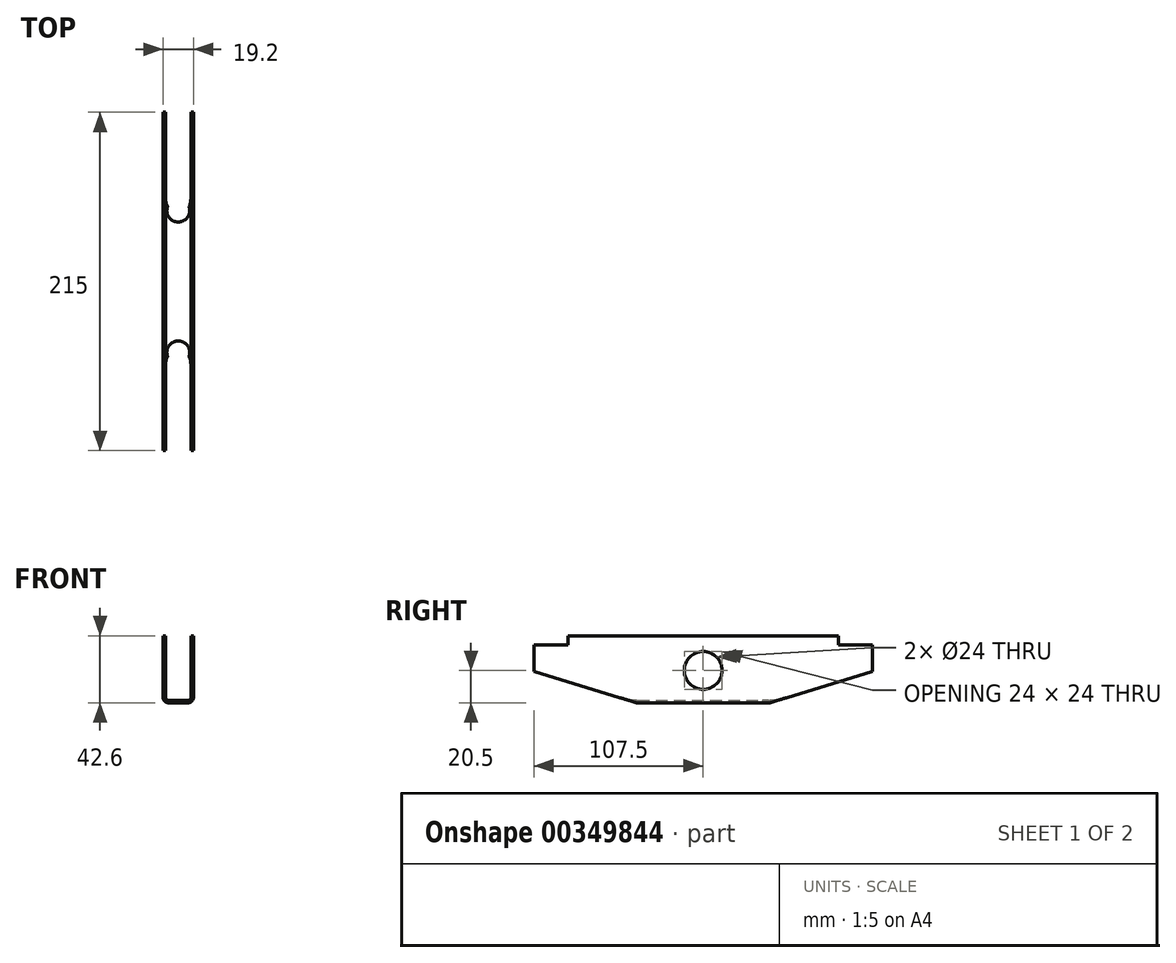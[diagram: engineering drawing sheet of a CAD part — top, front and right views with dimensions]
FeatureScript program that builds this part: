
annotation { "Feature Type Name" : "Feature", "Feature Type Description" : "" }
export const myFeature = defineFeature(function(context is Context, id is Id, definition is map)
    precondition{}
    {
        {
            var Q0;
            Q0=qCreatedBy(makeId("Front.planeOp"),FACE);
            var sketch = newSketch(context, id + "F0", { "sketchPlane" : qUnion([Q0])});
            skLineSegment(sketch, "E0", {"start": v(0, 0) * mm, "end": v(-6.4, 0) * mm});
            skLineSegment(sketch, "E1", {"start": v(-9.6, 3.2) * mm, "end": v(-9.6, 42.6) * mm});
            skLineSegment(sketch, "E2", {"start": v(-9.6, 42.6) * mm, "end": v(-8, 42.6) * mm});
            skLineSegment(sketch, "E3", {"start": v(-8, 42.6) * mm, "end": v(-8, 3.2) * mm});
            skLineSegment(sketch, "E4", {"start": v(-6.4, 1.6) * mm, "end": v(0, 1.6) * mm});
            skPoint(sketch, "E5.visualSharp", {"position": v(-8, 1.6) * mm});
            skArc(sketch, "E5.filletArc", {"start": v(-8, 3.2) * mm, "mid": v(-7.53, 2.07) * mm, "end": v(-6.4, 1.6) * mm});
            skPoint(sketch, "E6.visualSharp", {"position": v(-9.6, 0) * mm});
            skArc(sketch, "E6.filletArc", {"start": v(-9.6, 3.2) * mm, "mid": v(-8.66, 0.94) * mm, "end": v(-6.4, 0) * mm});
            skLineSegment(sketch, "E7", {"start": v(0, 0) * mm, "end": v(0, 33.76) * mm, "construction": true});
            skLineSegment(sketch, "E8.MirrorCS", {"start": v(9.6, 42.6) * mm, "end": v(8, 42.6) * mm});
            skArc(sketch, "E9.MirrorCS", {"start": v(8, 3.2) * mm, "mid": v(7.53, 2.07) * mm, "end": v(6.4, 1.6) * mm});
            skArc(sketch, "E10.MirrorCS", {"start": v(9.6, 3.2) * mm, "mid": v(8.66, 0.94) * mm, "end": v(6.4, 0) * mm});
            skLineSegment(sketch, "E11.MirrorCS", {"start": v(0, 0) * mm, "end": v(6.4, 0) * mm});
            skLineSegment(sketch, "E12.MirrorCS", {"start": v(9.6, 3.2) * mm, "end": v(9.6, 42.6) * mm});
            skPoint(sketch, "E13.MirrorP", {"position": v(8, 1.6) * mm});
            skPoint(sketch, "E14.MirrorP", {"position": v(9.6, 0) * mm});
            skLineSegment(sketch, "E15.MirrorCS", {"start": v(8, 42.6) * mm, "end": v(8, 3.2) * mm});
            skLineSegment(sketch, "E16.MirrorCS", {"start": v(6.4, 1.6) * mm, "end": v(0, 1.6) * mm});
            skSolve(sketch);
        }
        {
            var Q0;
            Q0 = qSketchRegion(id + "F0", true);
            extrude(context, id + "F1", {"entities" : qUnion([Q0]), "endBound" : BoundingType.SYMMETRIC, "depth" : 215 * mm});
        }
        {
            var Q0;
            Q0=makeQuery(id+"F1.opExtrude","SWEPT_FACE",FACE,{"disambiguationData":[OSD([sQuery(id+"F0.wireOp",EDGE,"E1")])]});
            var sketch = newSketch(context, id + "F2", { "sketchPlane" : qUnion([Q0])});
            skLineSegment(sketch, "E17.bottom", {"start": v(-107.5, 42.6) * mm, "end": v(-86, 42.6) * mm});
            skLineSegment(sketch, "E17.top", {"start": v(-107.5, 36.6) * mm, "end": v(-86, 36.6) * mm});
            skLineSegment(sketch, "E17.left", {"start": v(-107.5, 42.6) * mm, "end": v(-107.5, 36.6) * mm});
            skLineSegment(sketch, "E17.right", {"start": v(-86, 42.6) * mm, "end": v(-86, 36.6) * mm});
            skLineSegment(sketch, "E18", {"start": v(-107.5, 20) * mm, "end": v(-42.5, 0) * mm});
            skLineSegment(sketch, "E19", {"start": v(-42.5, 0) * mm, "end": v(-107.5, 0) * mm});
            skLineSegment(sketch, "E20", {"start": v(-107.5, 0) * mm, "end": v(-107.5, 20) * mm});
            skLineSegment(sketch, "E21", {"start": v(0, 0) * mm, "end": v(0, 57.1) * mm, "construction": true});
            skLineSegment(sketch, "E22.MirrorCS", {"start": v(107.5, 0) * mm, "end": v(107.5, 20) * mm});
            skLineSegment(sketch, "E23.MirrorCS", {"start": v(42.5, 0) * mm, "end": v(107.5, 0) * mm});
            skLineSegment(sketch, "E24.MirrorCS", {"start": v(107.5, 20) * mm, "end": v(42.5, 0) * mm});
            skLineSegment(sketch, "E25.MirrorCS", {"start": v(86, 42.6) * mm, "end": v(86, 36.6) * mm});
            skLineSegment(sketch, "E26.MirrorCS", {"start": v(107.5, 42.6) * mm, "end": v(107.5, 36.6) * mm});
            skLineSegment(sketch, "E27.MirrorCS", {"start": v(107.5, 42.6) * mm, "end": v(86, 42.6) * mm});
            skLineSegment(sketch, "E28.MirrorCS", {"start": v(107.5, 36.6) * mm, "end": v(86, 36.6) * mm});
            skCircle(sketch, "E29", {"center": v(0, 20.5) * mm, "radius": 12 * mm});
            skSolve(sketch);
        }
        {
            var Q0;
            Q0 = qSketchRegion(id + "F2", true);
            extrude(context, id + "F3", {"entities" : qUnion([Q0]), "operationType" : NewBodyOperationType.REMOVE, "oppositeDirection" : true, "depth" : 25 * mm});
        }
        {
            var Q0;
            Q0=makeQuery(id+"F1.opExtrude","SWEPT_FACE",FACE,{"disambiguationData":[OSD([sQuery(id+"F0.wireOp",EDGE,"E0"),sQuery(id+"F0.wireOp",EDGE,"E11.MirrorCS")])]});
            var sketch = newSketch(context, id + "F4", { "sketchPlane" : qUnion([Q0])});
            skLineSegment(sketch, "E30", {"start": v(0, 0) * mm, "end": v(0, -71.9) * mm, "construction": true});
            skCircle(sketch, "E31", {"center": v(0, -45) * mm, "radius": 7.25 * mm});
            skLineSegment(sketch, "E32", {"start": v(0, 0) * mm, "end": v(-19.35, 0) * mm, "construction": true});
            skCircle(sketch, "E33.MirrorC", {"center": v(0, 45) * mm, "radius": 7.25 * mm});
            skSolve(sketch);
        }
        {
            var Q0;
            Q0 = qSketchRegion(id + "F4", true);
            extrude(context, id + "F5", {"entities" : qUnion([Q0]), "operationType" : NewBodyOperationType.REMOVE, "oppositeDirection" : true, "depth" : 5 * mm});
        }
    });
